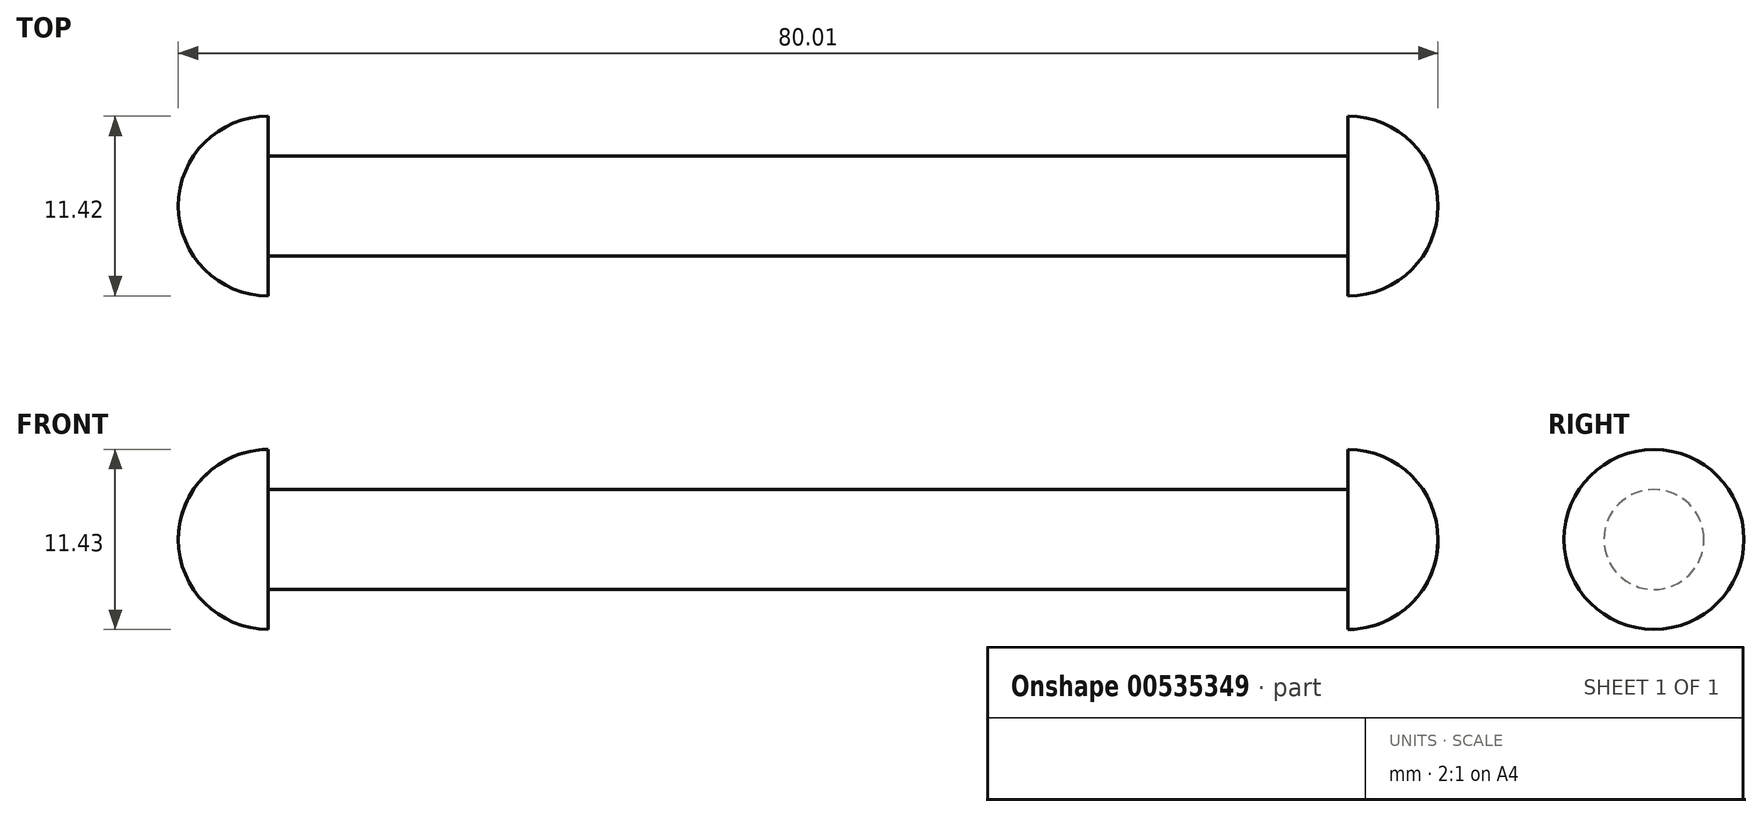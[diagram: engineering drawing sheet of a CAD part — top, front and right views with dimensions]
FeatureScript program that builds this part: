
annotation { "Feature Type Name" : "Feature", "Feature Type Description" : "" }
export const myFeature = defineFeature(function(context is Context, id is Id, definition is map)
    precondition{}
    {
        {
            var Q0;
            Q0=qCreatedBy(makeId("Front.planeOp"),FACE);
            var sketch = newSketch(context, id + "F0", { "sketchPlane" : qUnion([Q0])});
            skLineSegment(sketch, "E0", {"start": v(-74.3, 5.71) * mm, "end": v(-74.3, 3.18) * mm});
            skLineSegment(sketch, "E1", {"start": v(-74.3, 3.17) * mm, "end": v(-5.71, 3.17) * mm});
            skLineSegment(sketch, "E2", {"start": v(-5.72, 3.17) * mm, "end": v(-5.72, 5.72) * mm});
            skLineSegment(sketch, "E3", {"start": v(0, 0) * mm, "end": v(-80.01, 0) * mm});
            skArc(sketch, "E4", {"start": v(0, 0) * mm, "mid": v(-1.67, 4.04) * mm, "end": v(-5.72, 5.72) * mm});
            skArc(sketch, "E5", {"start": v(-74.3, 5.71) * mm, "mid": v(-78.34, 4.04) * mm, "end": v(-80.01, 0) * mm});
            skLineSegment(sketch, "E6", {"start": v(0, 0) * mm, "end": v(16.7, 0) * mm, "construction": true});
            skPoint(sketch, "E7", {"position": v(-40, 3.17) * mm});
            skSolve(sketch);
        }
        {
            var Q0;
            Q0=makeQuery(id+"F0.imprint","IMPRINT",FACE,{"disambiguationData":[TD([[makeQuery(id+"F0.imprint","IMPRINT",EDGE,{"derivedFrom":sQuery(id+"F0.wireOp",EDGE,"E0")}),-1.0]])]});
            var Q1;
            Q1=sQuery(id+"F0.wireOp",EDGE,"E6");
            revolve(context, id + "F1", {"entities" : qUnion([Q0]), "axis" : qUnion([Q1]), "revolveType" : RevolveType.FULL});
        }
    });
